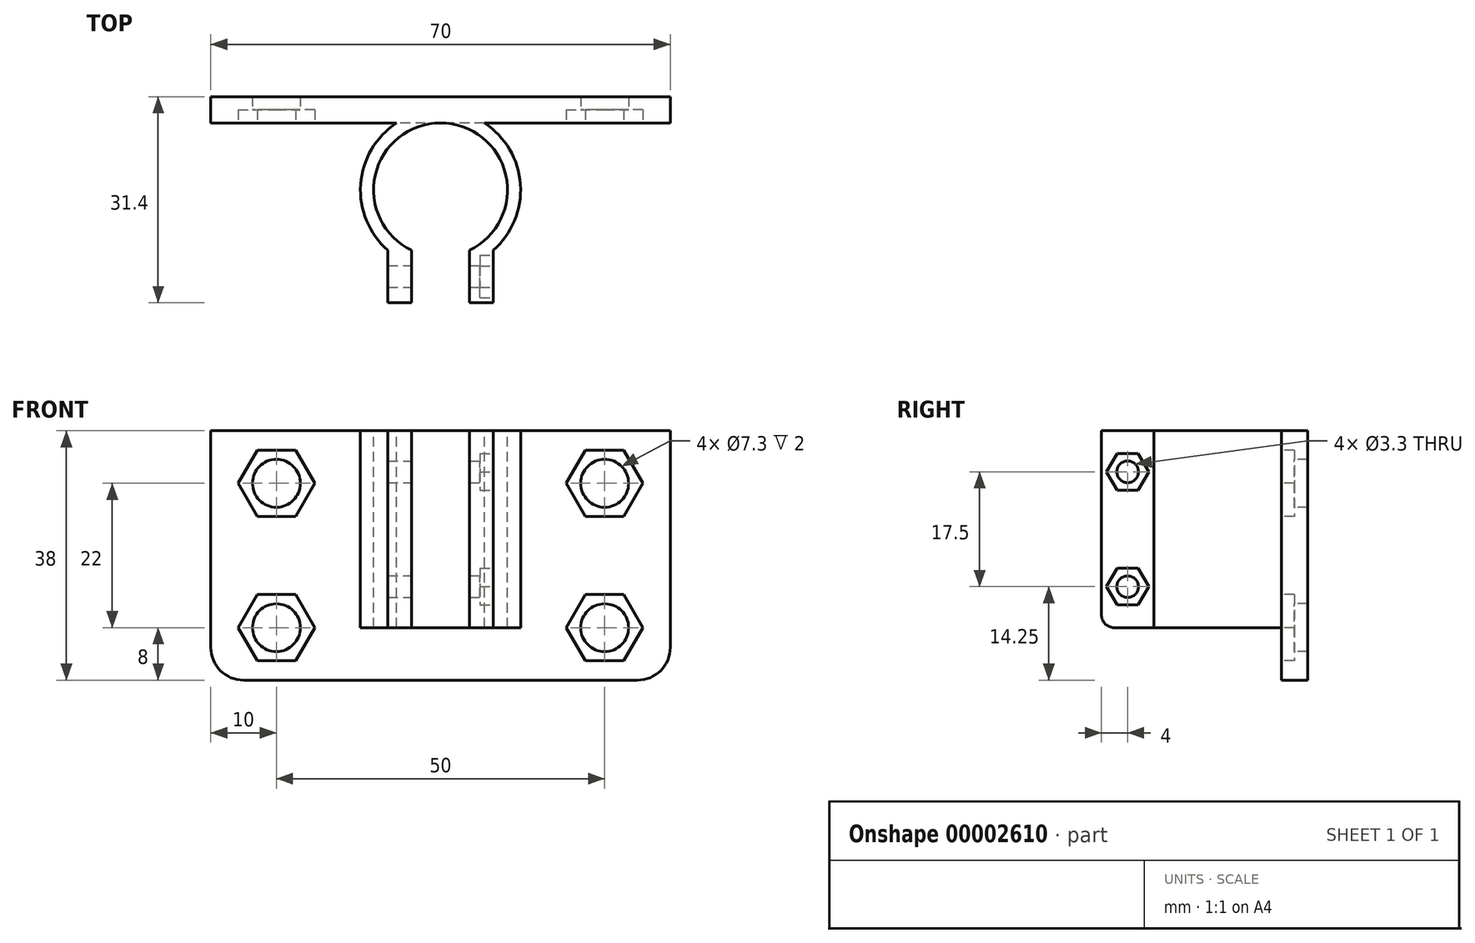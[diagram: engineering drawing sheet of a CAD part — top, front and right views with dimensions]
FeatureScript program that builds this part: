
annotation { "Feature Type Name" : "Feature", "Feature Type Description" : "" }
export const myFeature = defineFeature(function(context is Context, id is Id, definition is map)
    precondition{}
    {
        {
            var Q0;
            Q0=qCreatedBy(makeId("Front.planeOp"),FACE);
            var sketch = newSketch(context, id + "F0", { "sketchPlane" : qUnion([Q0])});
            skLineSegment(sketch, "E0.rect.bottom", {"start": v(35, -18) * mm, "end": v(-35, -18) * mm});
            skLineSegment(sketch, "E0.rect.top", {"start": v(35, 18) * mm, "end": v(-35, 18) * mm});
            skLineSegment(sketch, "E0.rect.left", {"start": v(35, -18) * mm, "end": v(35, 18) * mm});
            skLineSegment(sketch, "E0.rect.right", {"start": v(-35, -18) * mm, "end": v(-35, 18) * mm});
            skPoint(sketch, "E0.rect.middle", {"position": v(0, 0) * mm});
            skLineSegment(sketch, "E1.top", {"start": v(35, -20) * mm, "end": v(-35, -20) * mm});
            skLineSegment(sketch, "E1.left", {"start": v(35, -18) * mm, "end": v(35, -20) * mm});
            skLineSegment(sketch, "E1.right", {"start": v(-35, -18) * mm, "end": v(-35, -20) * mm});
            skSolve(sketch);
        }
        {
            var Q0;
            {var subQ0=makeQuery(id+"F0.imprint","IMPRINT",EDGE,{"derivedFrom":sQuery(id+"F0.wireOp",EDGE,"E0.rect.bottom")});Q0=qUnion([makeQuery(id+"F0.imprint","IMPRINT",FACE,{"disambiguationData":[TD([[makeQuery(id+"F0.imprint","IMPRINT",EDGE,{"derivedFrom":sQuery(id+"F0.wireOp",EDGE,"E0.rect.top")}),1.0]])]}),makeQuery(id+"F0.imprint","IMPRINT",FACE,{"disambiguationData":[TD([[subQ0,1.0]])]})]);}
            extrude(context, id + "F1", {"entities" : qUnion([Q0]), "depth" : 7 * mm});
        }
        {
            var Q0;
            Q0=makeQuery(id+"F1.opExtrude","SWEPT_FACE",FACE,{"disambiguationData":[OSD([sQuery(id+"F0.wireOp",EDGE,"E0.rect.top")])]});
            var sketch = newSketch(context, id + "F2", { "sketchPlane" : qUnion([Q0])});
            skPoint(sketch, "E2.rect.middle", {"position": v(0, 0) * mm});
            skLineSegment(sketch, "E3", {"start": v(0, 0) * mm, "end": v(0, -7) * mm, "construction": true});
            skLineSegment(sketch, "E4", {"start": v(0, -7) * mm, "end": v(0, -17.2) * mm, "construction": true});
            skCircle(sketch, "E5", {"center": v(0, -17.2) * mm, "radius": 10.2 * mm});
            skLineSegment(sketch, "E6", {"start": v(0, -17.2) * mm, "end": v(-12.2, -17.2) * mm, "construction": true});
            skCircle(sketch, "E7", {"center": v(0, -17.2) * mm, "radius": 12.2 * mm});
            skSolve(sketch);
        }
        {
            var Q0;
            {var subQ0=makeQuery(id+"F1.opExtrude","CAP_EDGE",EDGE,{"disambiguationData":[OSD([sQuery(id+"F0.wireOp",EDGE,"E0.rect.top")])],"isStart":false});var subQ1=sQuery(id+"F2.wireOp",EDGE,"E7");var subQ4=makeQuery(id+"F2.imprint","INTERSECT",VERTEX,{"disambiguationData":[OD(0.0)],"derivedFrom":[subQ0,subQ1]});Q0=makeQuery(id+"F2.imprint","IMPRINT",FACE,{"disambiguationData":[TD([[makeQuery(id+"F2.imprint","IMPRINT",EDGE,{"disambiguationData":[TD([[subQ4,-1.0]])],"derivedFrom":subQ1}),1.0]])]});}
            var Q1;
            {var subQ3=sQuery(id+"F2.wireOp",EDGE,"E5");Q1=makeQuery(id+"F2.imprint","IMPRINT",FACE,{"disambiguationData":[TD([[makeQuery(id+"F2.imprint","IMPRINT",EDGE,{"derivedFrom":subQ3}),-1.0]])]});}
            extrude(context, id + "F3", {"entities" : qUnion([Q0, Q1]), "operationType" : NewBodyOperationType.ADD, "oppositeDirection" : true, "depth" : 30 * mm});
        }
        {
            var Q0;
            Q0=makeQuery(id+"F3.boolean.opBoolean","MERGE",FACE,{"derivedFrom":[makeQuery(id+"F1.opExtrude","SWEPT_FACE",FACE,{"disambiguationData":[OSD([sQuery(id+"F0.wireOp",EDGE,"E0.rect.top")])]}),makeQuery(id+"F3.opExtrude","CAP_FACE",FACE,{"disambiguationData":[OSD([sQuery(id+"F2.wireOp",EDGE,"E5"),sQuery(id+"F2.wireOp",EDGE,"E7")])],"isStart":true})]});
            var sketch = newSketch(context, id + "F4", { "sketchPlane" : qUnion([Q0])});
            skLineSegment(sketch, "E8", {"start": v(0, 0) * mm, "end": v(0, -27.4) * mm, "construction": true});
            skLineSegment(sketch, "E9", {"start": v(0, -27.4) * mm, "end": v(0, -26.4) * mm, "construction": true});
            skLineSegment(sketch, "E10", {"start": v(0, -26.4) * mm, "end": v(12.94, -26.4) * mm, "construction": true});
            skLineSegment(sketch, "E11", {"start": v(12.94, -26.4) * mm, "end": v(12.94, -30.6) * mm, "construction": true});
            skLineSegment(sketch, "E12", {"start": v(12.94, -30.6) * mm, "end": v(-12.45, -30.6) * mm, "construction": true});
            skLineSegment(sketch, "E13.bottom", {"start": v(12.94, -26.4) * mm, "end": v(-12.45, -26.4) * mm});
            skLineSegment(sketch, "E13.top", {"start": v(12.94, -30.6) * mm, "end": v(-12.45, -30.6) * mm});
            skLineSegment(sketch, "E13.left", {"start": v(12.94, -26.4) * mm, "end": v(12.94, -30.6) * mm});
            skLineSegment(sketch, "E13.right", {"start": v(-12.45, -26.4) * mm, "end": v(-12.45, -30.6) * mm});
            skSolve(sketch);
        }
        {
            var Q0;
            {var subQ0=makeQuery(id+"F3.opExtrude","CAP_EDGE",EDGE,{"disambiguationData":[OSD([sQuery(id+"F2.wireOp",EDGE,"E7")])],"isStart":true});var subQ1=sQuery(id+"F4.wireOp",EDGE,"E13.bottom");var subQ3=makeQuery(id+"F4.imprint","INTERSECT",VERTEX,{"disambiguationData":[OD(0.0)],"derivedFrom":[subQ0,subQ1]});var subQ7=makeQuery(id+"F3.opExtrude","CAP_EDGE",EDGE,{"disambiguationData":[OSD([sQuery(id+"F2.wireOp",EDGE,"E5")])],"isStart":true});var subQ9=makeQuery(id+"F4.imprint","INTERSECT",VERTEX,{"disambiguationData":[OD(0.0)],"derivedFrom":[subQ7,subQ1]});Q0=qUnion([makeQuery(id+"F4.imprint","IMPRINT",FACE,{"disambiguationData":[TD([[makeQuery(id+"F4.imprint","IMPRINT",EDGE,{"derivedFrom":sQuery(id+"F4.wireOp",EDGE,"E13.top")}),-1.0]])]}),makeQuery(id+"F4.imprint","IMPRINT",FACE,{"disambiguationData":[TD([[makeQuery(id+"F4.imprint","IMPRINT",EDGE,{"disambiguationData":[TD([[subQ3,-1.0]])],"derivedFrom":subQ1}),1.0]])]}),makeQuery(id+"F4.imprint","IMPRINT",FACE,{"disambiguationData":[TD([[makeQuery(id+"F4.imprint","IMPRINT",EDGE,{"disambiguationData":[TD([[subQ9,-1.0]])],"derivedFrom":subQ1}),1.0]])]})]);}
            extrude(context, id + "F5", {"entities" : qUnion([Q0]), "operationType" : NewBodyOperationType.REMOVE, "oppositeDirection" : true, "depth" : 30 * mm});
        }
        {
            var Q0;
            Q0=makeQuery(id+"F1.opExtrude","CAP_FACE",FACE,{"disambiguationData":[OSD([sQuery(id+"F0.wireOp",EDGE,"E0.rect.top"),sQuery(id+"F0.wireOp",EDGE,"E0.rect.left"),sQuery(id+"F0.wireOp",EDGE,"E0.rect.right"),sQuery(id+"F0.wireOp",EDGE,"E1.top"),sQuery(id+"F0.wireOp",EDGE,"E1.left"),sQuery(id+"F0.wireOp",EDGE,"E1.right")])],"isStart":true});
            var sketch = newSketch(context, id + "F6", { "sketchPlane" : qUnion([Q0])});
            skLineSegment(sketch, "E14.bottom", {"start": v(35, 18) * mm, "end": v(-35, 18) * mm});
            skLineSegment(sketch, "E14.top", {"start": v(35, -20) * mm, "end": v(-35, -20) * mm});
            skLineSegment(sketch, "E14.left", {"start": v(35, 18) * mm, "end": v(35, -20) * mm});
            skLineSegment(sketch, "E14.right", {"start": v(-35, 18) * mm, "end": v(-35, -20) * mm});
            skSolve(sketch);
        }
        {
            var Q0;
            Q0=qSketchRegion(id+"F6",true);
            extrude(context, id + "F7", {"entities" : qUnion([Q0]), "operationType" : NewBodyOperationType.ADD, "depth" : 2 * mm});
        }
        {
            var Q0;
            Q0=makeQuery(id+"F5.boolean.opBoolean","COPY",FACE,{"disambiguationData":[OD(1.0)],"derivedFrom":makeQuery(id+"F5.opExtrude","SWEPT_FACE",FACE,{"disambiguationData":[OSD([sQuery(id+"F4.wireOp",EDGE,"E13.bottom")])]})});
            var sketch = newSketch(context, id + "F8", { "sketchPlane" : qUnion([Q0])});
            skLineSegment(sketch, "E15.bottom", {"start": v(-8.01, 18) * mm, "end": v(-4.4, 18) * mm});
            skLineSegment(sketch, "E15.top", {"start": v(-8.01, -12) * mm, "end": v(-4.4, -12) * mm});
            skLineSegment(sketch, "E15.left", {"start": v(-8.01, 18) * mm, "end": v(-8.01, -12) * mm});
            skLineSegment(sketch, "E15.right", {"start": v(-4.4, 18) * mm, "end": v(-4.4, -12) * mm});
            skSolve(sketch);
        }
        {
            var Q0;
            Q0=makeQuery(id+"F8.imprint","IMPRINT",FACE,{"disambiguationData":[TD([[makeQuery(id+"F8.imprint","IMPRINT",EDGE,{"derivedFrom":sQuery(id+"F8.wireOp",EDGE,"E15.bottom")}),1.0]])]});
            extrude(context, id + "F9", {"entities" : qUnion([Q0]), "operationType" : NewBodyOperationType.ADD, "depth" : 8 * mm});
        }
        {
            var Q0;
            Q0=makeQuery(id+"F5.boolean.opBoolean","COPY",FACE,{"disambiguationData":[OD(0.0)],"derivedFrom":makeQuery(id+"F5.opExtrude","SWEPT_FACE",FACE,{"disambiguationData":[OSD([sQuery(id+"F4.wireOp",EDGE,"E13.bottom")])]})});
            var sketch = newSketch(context, id + "F10", { "sketchPlane" : qUnion([Q0])});
            skLineSegment(sketch, "E16.bottom", {"start": v(4.4, 18) * mm, "end": v(8.01, 18) * mm});
            skLineSegment(sketch, "E16.top", {"start": v(4.4, -12) * mm, "end": v(8.01, -12) * mm});
            skLineSegment(sketch, "E16.left", {"start": v(4.4, 18) * mm, "end": v(4.4, -12) * mm});
            skLineSegment(sketch, "E16.right", {"start": v(8.01, 18) * mm, "end": v(8.01, -12) * mm});
            skSolve(sketch);
        }
        {
            var Q0;
            Q0 = qSketchRegion(id + "F10", true);
            extrude(context, id + "F11", {"entities" : qUnion([Q0]), "operationType" : NewBodyOperationType.ADD, "depth" : 8 * mm});
        }
        {
            var Q0;
            Q0=makeQuery(id+"F11.opExtrude","SWEPT_FACE",FACE,{"disambiguationData":[OSD([sQuery(id+"F10.wireOp",EDGE,"E16.right")])]});
            var sketch = newSketch(context, id + "F12", { "sketchPlane" : qUnion([Q0])});
            skLineSegment(sketch, "E17", {"start": v(-26.4, -12) * mm, "end": v(-26.4, -5.75) * mm, "construction": true});
            skLineSegment(sketch, "E18", {"start": v(-26.4, 18) * mm, "end": v(-26.4, 11.75) * mm, "construction": true});
            skLineSegment(sketch, "E19", {"start": v(-26.4, 11.75) * mm, "end": v(-30.4, 11.75) * mm, "construction": true});
            skLineSegment(sketch, "E20", {"start": v(-26.4, -5.75) * mm, "end": v(-30.4, -5.75) * mm, "construction": true});
            skCircle(sketch, "E21", {"center": v(-30.4, -5.75) * mm, "radius": 1.65 * mm});
            skCircle(sketch, "E22", {"center": v(-30.4, 11.75) * mm, "radius": 1.65 * mm});
            skSolve(sketch);
        }
        {
            var Q0;
            Q0 = qSketchRegion(id + "F12", true);
            extrude(context, id + "F13", {"entities" : qUnion([Q0]), "operationType" : NewBodyOperationType.REMOVE, "oppositeDirection" : true, "depth" : 25 * mm});
        }
        {
            var Q0;
            Q0=makeQuery(id+"F1.opExtrude","CAP_FACE",FACE,{"disambiguationData":[OSD([sQuery(id+"F0.wireOp",EDGE,"E0.rect.top"),sQuery(id+"F0.wireOp",EDGE,"E0.rect.left"),sQuery(id+"F0.wireOp",EDGE,"E0.rect.right"),sQuery(id+"F0.wireOp",EDGE,"E1.top"),sQuery(id+"F0.wireOp",EDGE,"E1.left"),sQuery(id+"F0.wireOp",EDGE,"E1.right")])],"isStart":false});
            var sketch = newSketch(context, id + "F14", { "sketchPlane" : qUnion([Q0])});
            skLineSegment(sketch, "E23", {"start": v(35, 18) * mm, "end": v(25, 18) * mm, "construction": true});
            skLineSegment(sketch, "E24", {"start": v(25, 18) * mm, "end": v(25, 10) * mm, "construction": true});
            skLineSegment(sketch, "E25", {"start": v(25, 10) * mm, "end": v(25, -12) * mm, "construction": true});
            skPoint(sketch, "E26.rect.middle", {"position": v(25, 10) * mm});
            skPoint(sketch, "E27.rect.middle", {"position": v(25, -12) * mm});
            skLineSegment(sketch, "E28", {"start": v(-35, 18) * mm, "end": v(-25, 18) * mm, "construction": true});
            skLineSegment(sketch, "E29", {"start": v(-25, 18) * mm, "end": v(-25, 10) * mm, "construction": true});
            skLineSegment(sketch, "E30", {"start": v(-25, 10) * mm, "end": v(-25, -12) * mm, "construction": true});
            skPoint(sketch, "E31.rect.middle", {"position": v(-25, 10) * mm});
            skPoint(sketch, "E32.rect.middle", {"position": v(-25, -12) * mm});
            skCircle(sketch, "E33", {"center": v(25, 10) * mm, "radius": 3.65 * mm});
            skCircle(sketch, "E34", {"center": v(25, -12) * mm, "radius": 3.65 * mm});
            skCircle(sketch, "E35", {"center": v(-25, 10) * mm, "radius": 3.65 * mm});
            skCircle(sketch, "E36", {"center": v(-25, -12) * mm, "radius": 3.65 * mm});
            skSolve(sketch);
        }
        {
            var Q0;
            Q0=qSketchRegion(id+"F14",true);
            extrude(context, id + "F15", {"entities" : qUnion([Q0]), "operationType" : NewBodyOperationType.REMOVE, "oppositeDirection" : true, "depth" : 9 * mm});
        }
        {
            var Q0;
            Q0=makeQuery(id+"F11.opExtrude","SWEPT_FACE",FACE,{"disambiguationData":[OSD([sQuery(id+"F10.wireOp",EDGE,"E16.right")])]});
            var sketch = newSketch(context, id + "F16", { "sketchPlane" : qUnion([Q0])});
            skCircle(sketch, "E37", {"center": v(-30.4, -5.75) * mm, "radius": 2.8 * mm, "construction": true});
            skLineSegment(sketch, "E38.0", {"start": v(-28.78, -8.55) * mm, "end": v(-32.02, -8.55) * mm});
            skLineSegment(sketch, "E38.1", {"start": v(-32.02, -8.55) * mm, "end": v(-33.63, -5.75) * mm});
            skLineSegment(sketch, "E38.2", {"start": v(-33.63, -5.75) * mm, "end": v(-32.02, -2.95) * mm});
            skLineSegment(sketch, "E38.3", {"start": v(-32.02, -2.95) * mm, "end": v(-28.78, -2.95) * mm});
            skLineSegment(sketch, "E38.4", {"start": v(-28.78, -2.95) * mm, "end": v(-27.17, -5.75) * mm});
            skLineSegment(sketch, "E38.5", {"start": v(-27.17, -5.75) * mm, "end": v(-28.78, -8.55) * mm});
            skPoint(sketch, "E38.0.midPoint", {"position": v(-30.4, -8.55) * mm});
            skCircle(sketch, "E39", {"center": v(-30.4, 11.75) * mm, "radius": 2.8 * mm, "construction": true});
            skLineSegment(sketch, "E40.0", {"start": v(-28.78, 8.95) * mm, "end": v(-32.02, 8.95) * mm});
            skLineSegment(sketch, "E40.1", {"start": v(-32.02, 8.95) * mm, "end": v(-33.63, 11.75) * mm});
            skLineSegment(sketch, "E40.2", {"start": v(-33.63, 11.75) * mm, "end": v(-32.02, 14.55) * mm});
            skLineSegment(sketch, "E40.3", {"start": v(-32.02, 14.55) * mm, "end": v(-28.78, 14.55) * mm});
            skLineSegment(sketch, "E40.4", {"start": v(-28.78, 14.55) * mm, "end": v(-27.17, 11.75) * mm});
            skLineSegment(sketch, "E40.5", {"start": v(-27.17, 11.75) * mm, "end": v(-28.78, 8.95) * mm});
            skPoint(sketch, "E40.0.midPoint", {"position": v(-30.4, 8.95) * mm});
            skSolve(sketch);
        }
        {
            var Q0;
            Q0=qSketchRegion(id+"F16",true);
            extrude(context, id + "F17", {"entities" : qUnion([Q0]), "operationType" : NewBodyOperationType.REMOVE, "oppositeDirection" : true, "depth" : 2 * mm});
        }
        {
            var Q0;
            Q0=makeQuery(id+"F1.opExtrude","CAP_FACE",FACE,{"disambiguationData":[OSD([sQuery(id+"F0.wireOp",EDGE,"E0.rect.top"),sQuery(id+"F0.wireOp",EDGE,"E0.rect.left"),sQuery(id+"F0.wireOp",EDGE,"E0.rect.right"),sQuery(id+"F0.wireOp",EDGE,"E1.top"),sQuery(id+"F0.wireOp",EDGE,"E1.left"),sQuery(id+"F0.wireOp",EDGE,"E1.right")])],"isStart":false});
            var sketch = newSketch(context, id + "F18", { "sketchPlane" : qUnion([Q0])});
            skCircle(sketch, "E41", {"center": v(25, -12) * mm, "radius": 5.05 * mm, "construction": true});
            skCircle(sketch, "E42", {"center": v(-25, 10) * mm, "radius": 5.05 * mm, "construction": true});
            skCircle(sketch, "E43", {"center": v(-25, -12) * mm, "radius": 5.05 * mm, "construction": true});
            skLineSegment(sketch, "E44.0", {"start": v(27.92, -17.05) * mm, "end": v(22.08, -17.05) * mm});
            skLineSegment(sketch, "E44.1", {"start": v(22.08, -17.05) * mm, "end": v(19.17, -12) * mm});
            skLineSegment(sketch, "E44.2", {"start": v(19.17, -12) * mm, "end": v(22.08, -6.95) * mm});
            skLineSegment(sketch, "E44.3", {"start": v(22.08, -6.95) * mm, "end": v(27.92, -6.95) * mm});
            skLineSegment(sketch, "E44.4", {"start": v(27.92, -6.95) * mm, "end": v(30.83, -12) * mm});
            skLineSegment(sketch, "E44.5", {"start": v(30.83, -12) * mm, "end": v(27.92, -17.05) * mm});
            skPoint(sketch, "E44.0.midPoint", {"position": v(25, -17.05) * mm});
            skLineSegment(sketch, "E45.0", {"start": v(-22.08, 4.95) * mm, "end": v(-27.92, 4.95) * mm});
            skLineSegment(sketch, "E45.1", {"start": v(-27.92, 4.95) * mm, "end": v(-30.83, 10) * mm});
            skLineSegment(sketch, "E45.2", {"start": v(-30.83, 10) * mm, "end": v(-27.92, 15.05) * mm});
            skLineSegment(sketch, "E45.3", {"start": v(-27.92, 15.05) * mm, "end": v(-22.08, 15.05) * mm});
            skLineSegment(sketch, "E45.4", {"start": v(-22.08, 15.05) * mm, "end": v(-19.17, 10) * mm});
            skLineSegment(sketch, "E45.5", {"start": v(-19.17, 10) * mm, "end": v(-22.08, 4.95) * mm});
            skPoint(sketch, "E45.0.midPoint", {"position": v(-25, 4.95) * mm});
            skLineSegment(sketch, "E46.0", {"start": v(-22.08, -17.05) * mm, "end": v(-27.92, -17.05) * mm});
            skLineSegment(sketch, "E46.1", {"start": v(-27.92, -17.05) * mm, "end": v(-30.83, -12) * mm});
            skLineSegment(sketch, "E46.2", {"start": v(-30.83, -12) * mm, "end": v(-27.92, -6.95) * mm});
            skLineSegment(sketch, "E46.3", {"start": v(-27.92, -6.95) * mm, "end": v(-22.08, -6.95) * mm});
            skLineSegment(sketch, "E46.4", {"start": v(-22.08, -6.95) * mm, "end": v(-19.17, -12) * mm});
            skLineSegment(sketch, "E46.5", {"start": v(-19.17, -12) * mm, "end": v(-22.08, -17.05) * mm});
            skPoint(sketch, "E46.0.midPoint", {"position": v(-25, -17.05) * mm});
            skCircle(sketch, "E47", {"center": v(25, 10) * mm, "radius": 5.05 * mm, "construction": true});
            skLineSegment(sketch, "E48.0", {"start": v(27.92, 4.95) * mm, "end": v(22.08, 4.95) * mm});
            skLineSegment(sketch, "E48.1", {"start": v(22.08, 4.95) * mm, "end": v(19.17, 10) * mm});
            skLineSegment(sketch, "E48.2", {"start": v(19.17, 10) * mm, "end": v(22.08, 15.05) * mm});
            skLineSegment(sketch, "E48.3", {"start": v(22.08, 15.05) * mm, "end": v(27.92, 15.05) * mm});
            skLineSegment(sketch, "E48.4", {"start": v(27.92, 15.05) * mm, "end": v(30.83, 10) * mm});
            skLineSegment(sketch, "E48.5", {"start": v(30.83, 10) * mm, "end": v(27.92, 4.95) * mm});
            skPoint(sketch, "E48.0.midPoint", {"position": v(25, 4.95) * mm});
            skSolve(sketch);
        }
        {
            var Q0;
            Q0=qSketchRegion(id+"F18",true);
            extrude(context, id + "F19", {"entities" : qUnion([Q0]), "operationType" : NewBodyOperationType.REMOVE, "oppositeDirection" : true, "depth" : 2 * mm});
        }
        {
            var Q0;
            Q0=makeQuery(id+"F9.opExtrude","CAP_EDGE",EDGE,{"disambiguationData":[OSD([sQuery(id+"F8.wireOp",EDGE,"E15.top")])],"isStart":false});
            var Q1;
            Q1=makeQuery(id+"F11.opExtrude","CAP_EDGE",EDGE,{"disambiguationData":[OSD([sQuery(id+"F10.wireOp",EDGE,"E16.top")])],"isStart":false});
            fillet(context, id + "F20", {"entities" : qUnion([Q0, Q1]), "radius" : 2 * mm, "tangentPropagation" : true, "allowEdgeOverflow" : false});
        }
        {
            var Q0;
            Q0=makeQuery(id+"F7.boolean.opBoolean","MERGE",EDGE,{"derivedFrom":[makeQuery(id+"F1.opExtrude","SWEPT_EDGE",EDGE,{"disambiguationData":[OSD([sQuery(id+"F0.wireOp",EDGE,"E1.top"),sQuery(id+"F0.wireOp",EDGE,"E1.right")])]}),makeQuery(id+"F7.opExtrude","SWEPT_EDGE",EDGE,{"disambiguationData":[OSD([sQuery(id+"F6.wireOp",EDGE,"E14.top"),sQuery(id+"F6.wireOp",EDGE,"E14.left")])]})]});
            var Q1;
            Q1=makeQuery(id+"F7.boolean.opBoolean","MERGE",EDGE,{"derivedFrom":[makeQuery(id+"F1.opExtrude","SWEPT_EDGE",EDGE,{"disambiguationData":[OSD([sQuery(id+"F0.wireOp",EDGE,"E1.top"),sQuery(id+"F0.wireOp",EDGE,"E1.left")])]}),makeQuery(id+"F7.opExtrude","SWEPT_EDGE",EDGE,{"disambiguationData":[OSD([sQuery(id+"F6.wireOp",EDGE,"E14.top"),sQuery(id+"F6.wireOp",EDGE,"E14.right")])]})]});
            fillet(context, id + "F21", {"entities" : qUnion([Q0, Q1]), "radius" : 5 * mm, "tangentPropagation" : true, "allowEdgeOverflow" : false});
        }
        {
            var Q0;
            Q0=makeQuery(id+"F7.opExtrude","CAP_FACE",FACE,{"disambiguationData":[OSD([sQuery(id+"F6.wireOp",EDGE,"E14.bottom"),sQuery(id+"F6.wireOp",EDGE,"E14.top"),sQuery(id+"F6.wireOp",EDGE,"E14.left"),sQuery(id+"F6.wireOp",EDGE,"E14.right")])],"isStart":false});
            var sketch = newSketch(context, id + "F22", { "sketchPlane" : qUnion([Q0])});
            skLineSegment(sketch, "E49.bottom", {"start": v(35, 18) * mm, "end": v(-35.08, 18) * mm});
            skLineSegment(sketch, "E49.top", {"start": v(35, -20.26) * mm, "end": v(-35.08, -20.26) * mm});
            skLineSegment(sketch, "E49.left", {"start": v(35, 18) * mm, "end": v(35, -20.26) * mm});
            skLineSegment(sketch, "E49.right", {"start": v(-35.08, 18) * mm, "end": v(-35.08, -20.26) * mm});
            skSolve(sketch);
        }
        {
            var Q0;
            Q0 = qSketchRegion(id + "F22", true);
            extrude(context, id + "F23", {"entities" : qUnion([Q0]), "operationType" : NewBodyOperationType.REMOVE, "oppositeDirection" : true, "depth" : 5 * mm});
        }
    });
